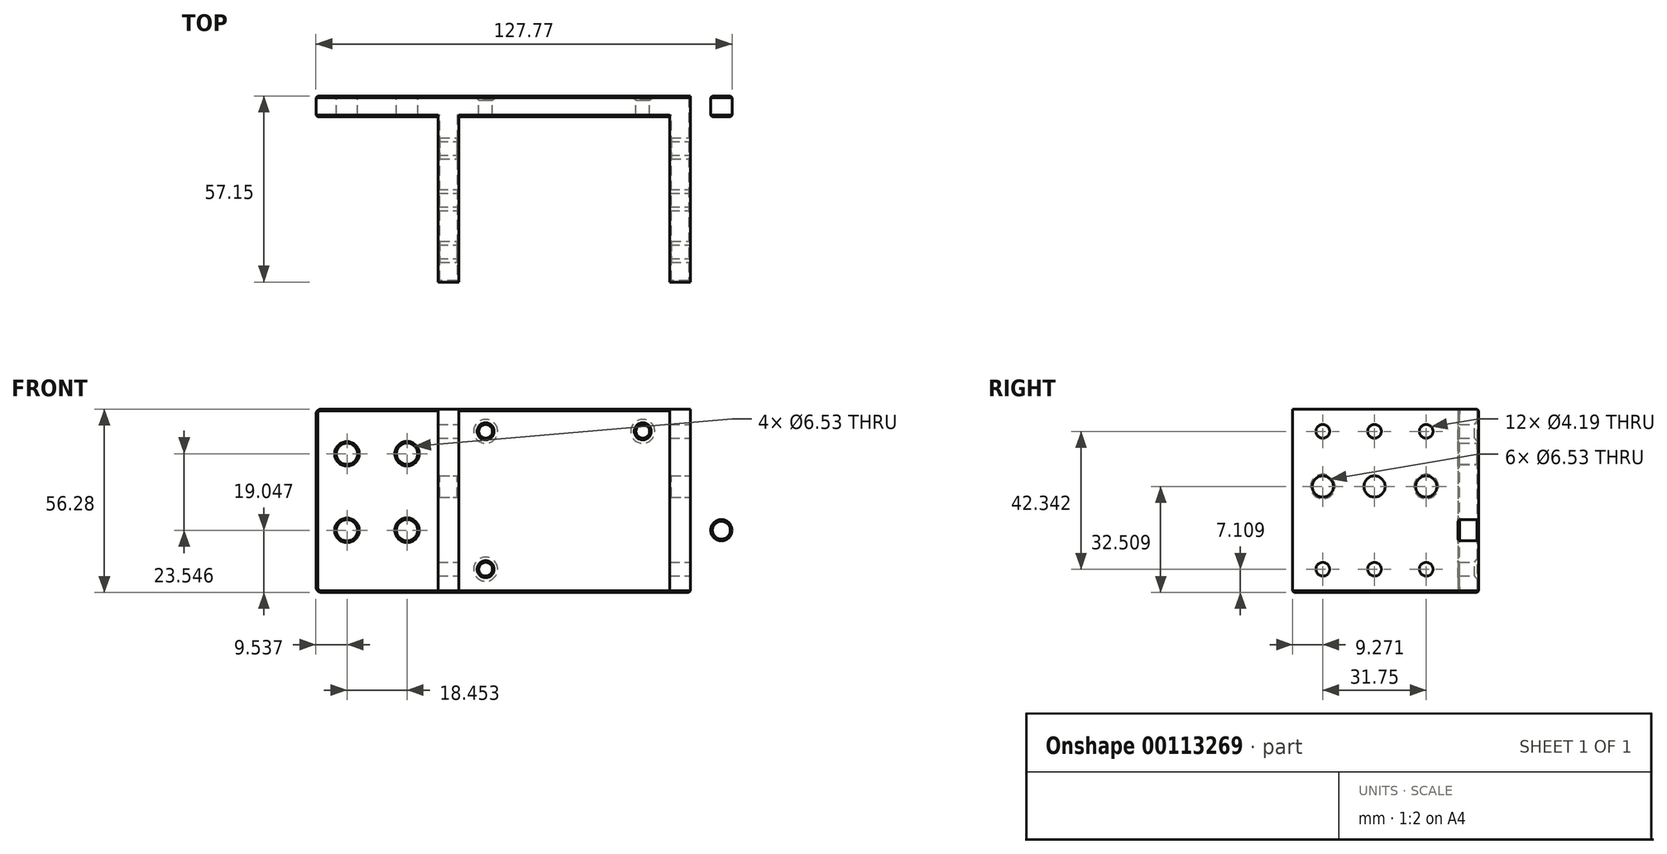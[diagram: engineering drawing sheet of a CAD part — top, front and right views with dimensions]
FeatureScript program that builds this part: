
annotation { "Feature Type Name" : "Feature", "Feature Type Description" : "" }
export const myFeature = defineFeature(function(context is Context, id is Id, definition is map)
    precondition{}
    {
        {
            var Q0;
            Q0=qCreatedBy(makeId("Front.planeOp"),FACE);
            var sketch = newSketch(context, id + "F0", { "sketchPlane" : qUnion([Q0])});
            skLineSegment(sketch, "E0.right", {"start": v(-76.2, -28.14) * mm, "end": v(-76.25, 28.14) * mm});
            skCircle(sketch, "E1", {"center": v(-24.13, 21.31) * mm, "radius": 2.1 * mm});
            skCircle(sketch, "E2", {"center": v(-24.13, -21.03) * mm, "radius": 2.1 * mm});
            skCircle(sketch, "E3", {"center": v(-66.71, -9.1) * mm, "radius": 3.26 * mm});
            skCircle(sketch, "E4", {"center": v(-66.71, 14.4) * mm, "radius": 3.26 * mm});
            skCircle(sketch, "E5", {"center": v(-48.26, -9.04) * mm, "radius": 3.26 * mm});
            skCircle(sketch, "E6", {"center": v(-48.26, 14.45) * mm, "radius": 3.26 * mm});
            skLineSegment(sketch, "E7.bottom", {"start": v(-38.74, 28.14) * mm, "end": v(-32.39, 28.14) * mm});
            skLineSegment(sketch, "E7.top", {"start": v(-38.74, -28.14) * mm, "end": v(-32.39, -28.14) * mm});
            skLineSegment(sketch, "E7.left", {"start": v(-38.74, 28.14) * mm, "end": v(-38.74, -28.14) * mm});
            skLineSegment(sketch, "E7.right", {"start": v(-32.39, 28.14) * mm, "end": v(-32.39, -28.14) * mm});
            skLineSegment(sketch, "E8.trimOffspring", {"start": v(-32.39, 28.14) * mm, "end": v(-76.25, 28.14) * mm});
            skLineSegment(sketch, "E9.trimOffspring", {"start": v(-32.39, -28.14) * mm, "end": v(-76.2, -28.14) * mm});
            skLineSegment(sketch, "E10.bottom", {"start": v(-32.39, 28.14) * mm, "end": v(0, 28.14) * mm});
            skLineSegment(sketch, "E10.top", {"start": v(-32.39, -28.14) * mm, "end": v(0, -28.14) * mm});
            skLineSegment(sketch, "E11.MirrorCS", {"start": v(38.74, -28.14) * mm, "end": v(32.39, -28.14) * mm});
            skLineSegment(sketch, "E12.MirrorCS", {"start": v(38.74, 28.14) * mm, "end": v(32.39, 28.14) * mm});
            skCircle(sketch, "E13.MirrorC", {"center": v(48.26, -9.04) * mm, "radius": 3.26 * mm});
            skCircle(sketch, "E14.MirrorC", {"center": v(66.71, 14.4) * mm, "radius": 3.26 * mm});
            skCircle(sketch, "E15.MirrorC", {"center": v(66.71, -9.1) * mm, "radius": 3.26 * mm});
            skCircle(sketch, "E16.MirrorC", {"center": v(24.13, -21.03) * mm, "radius": 2.1 * mm});
            skCircle(sketch, "E17.MirrorC", {"center": v(48.26, 14.45) * mm, "radius": 3.26 * mm});
            skLineSegment(sketch, "E18.MirrorCS", {"start": v(32.39, 28.14) * mm, "end": v(32.39, -28.14) * mm});
            skCircle(sketch, "E19.MirrorC", {"center": v(24.13, 21.31) * mm, "radius": 2.1 * mm});
            skLineSegment(sketch, "E20.MirrorCS", {"start": v(38.74, 28.14) * mm, "end": v(38.74, -28.14) * mm});
            skLineSegment(sketch, "E21.MirrorCS", {"start": v(32.39, 28.14) * mm, "end": v(0, 28.14) * mm});
            skLineSegment(sketch, "E22.MirrorCS", {"start": v(32.39, -28.14) * mm, "end": v(0, -28.14) * mm});
            skLineSegment(sketch, "E23.MirrorCS", {"start": v(32.39, 28.14) * mm, "end": v(76.25, 28.14) * mm});
            skLineSegment(sketch, "E24.MirrorCS", {"start": v(32.39, -28.14) * mm, "end": v(76.2, -28.14) * mm});
            skLineSegment(sketch, "E25.MirrorCS", {"start": v(76.2, -28.14) * mm, "end": v(76.25, 28.14) * mm});
            skSolve(sketch);
        }
        {
            var Q0;
            {var subQ0=sQuery(id+"F0.wireOp",EDGE,"E7.left");Q0=makeQuery(id+"F0.imprint","IMPRINT",FACE,{"disambiguationData":[TD([[makeQuery(id+"F0.imprint","IMPRINT",EDGE,{"derivedFrom":subQ0}),1.0]])]});}
            var Q1;
            {var subQ0=sQuery(id+"F0.wireOp",EDGE,"E18.MirrorCS");Q1=makeQuery(id+"F0.imprint","IMPRINT",FACE,{"disambiguationData":[TD([[makeQuery(id+"F0.imprint","IMPRINT",EDGE,{"derivedFrom":subQ0}),1.0]])]});}
            extrude(context, id + "F1", {"entities" : qUnion([Q0, Q1]), "depth" : 57.15 * mm});
        }
        {
            var Q0;
            {var subQ0=sQuery(id+"F0.wireOp",EDGE,"E0.right");Q0=makeQuery(id+"F0.imprint","IMPRINT",FACE,{"disambiguationData":[TD([[makeQuery(id+"F0.imprint","IMPRINT",EDGE,{"derivedFrom":subQ0}),-1.0]])]});}
            var Q1;
            Q1=makeQuery(id+"F0.imprint","IMPRINT",FACE,{"disambiguationData":[TD([[makeQuery(id+"F0.imprint","IMPRINT",EDGE,{"derivedFrom":sQuery(id+"F0.wireOp",EDGE,"E1")}),-1.0]])]});
            var Q2;
            Q2=makeQuery(id+"F0.imprint","IMPRINT",FACE,{"disambiguationData":[TD([[makeQuery(id+"F0.imprint","IMPRINT",EDGE,{"derivedFrom":sQuery(id+"F0.wireOp",EDGE,"E16.MirrorC")}),1.0]])]});
            var Q3;
            Q3=makeQuery(id+"F0.imprint","IMPRINT",FACE,{"disambiguationData":[TD([[makeQuery(id+"F0.imprint","IMPRINT",EDGE,{"derivedFrom":sQuery(id+"F0.wireOp",EDGE,"E13.MirrorC")}),1.0]])]});
            extrude(context, id + "F2", {"entities" : qUnion([Q0, Q1, Q2, Q3]), "depth" : 6.35 * mm});
        }
        {
            var Q0;
            Q0=makeQuery(id+"F1.opExtrude","SWEPT_BODY",BODY,{"disambiguationData":[OSD([sQuery(id+"F0.wireOp",EDGE,"E18.MirrorCS"),sQuery(id+"F0.wireOp",EDGE,"E20.MirrorCS"),sQuery(id+"F0.wireOp",EDGE,"E23.MirrorCS"),sQuery(id+"F0.wireOp",EDGE,"E24.MirrorCS")])]});
            var Q1;
            Q1=makeQuery(id+"F2.opExtrude","SWEPT_BODY",BODY,{"disambiguationData":[OSD([sQuery(id+"F0.wireOp",EDGE,"E0.right"),sQuery(id+"F0.wireOp",EDGE,"E3"),sQuery(id+"F0.wireOp",EDGE,"E4"),sQuery(id+"F0.wireOp",EDGE,"E5"),sQuery(id+"F0.wireOp",EDGE,"E6"),sQuery(id+"F0.wireOp",EDGE,"E7.left"),sQuery(id+"F0.wireOp",EDGE,"E8.trimOffspring"),sQuery(id+"F0.wireOp",EDGE,"E9.trimOffspring")])]});
            var Q2;
            Q2=makeQuery(id+"F1.opExtrude","SWEPT_BODY",BODY,{"disambiguationData":[OSD([sQuery(id+"F0.wireOp",EDGE,"E7.left"),sQuery(id+"F0.wireOp",EDGE,"E8.trimOffspring"),sQuery(id+"F0.wireOp",EDGE,"E9.trimOffspring"),sQuery(id+"F0.wireOp",EDGE,"E7.right")])]});
            var Q3;
            Q3=makeQuery(id+"F2.opExtrude","SWEPT_BODY",BODY,{"disambiguationData":[OSD([sQuery(id+"F0.wireOp",EDGE,"E1"),sQuery(id+"F0.wireOp",EDGE,"E2"),sQuery(id+"F0.wireOp",EDGE,"E10.bottom"),sQuery(id+"F0.wireOp",EDGE,"E10.top"),sQuery(id+"F0.wireOp",EDGE,"E7.right"),sQuery(id+"F0.wireOp",EDGE,"E16.MirrorC"),sQuery(id+"F0.wireOp",EDGE,"E19.MirrorC"),sQuery(id+"F0.wireOp",EDGE,"E18.MirrorCS"),sQuery(id+"F0.wireOp",EDGE,"E21.MirrorCS"),sQuery(id+"F0.wireOp",EDGE,"E22.MirrorCS")])]});
            var Q4;
            Q4=makeQuery(id+"F2.opExtrude","SWEPT_BODY",BODY,{"disambiguationData":[OSD([sQuery(id+"F0.wireOp",EDGE,"E13.MirrorC"),sQuery(id+"F0.wireOp",EDGE,"E14.MirrorC"),sQuery(id+"F0.wireOp",EDGE,"E15.MirrorC"),sQuery(id+"F0.wireOp",EDGE,"E17.MirrorC"),sQuery(id+"F0.wireOp",EDGE,"E20.MirrorCS"),sQuery(id+"F0.wireOp",EDGE,"E23.MirrorCS"),sQuery(id+"F0.wireOp",EDGE,"E24.MirrorCS"),sQuery(id+"F0.wireOp",EDGE,"E25.MirrorCS")])]});
            booleanBodies(context, id + "F3", {"operationType" : BooleanOperationType.UNION, "tools" : qUnion([Q0, Q1, Q2, Q3, Q4])});
        }
        {
            var Q0;
            Q0=makeQuery(id+"F2.opExtrude","CAP_EDGE",EDGE,{"disambiguationData":[OSD([sQuery(id+"F0.wireOp",EDGE,"E19.MirrorC")])],"isStart":true});
            var Q1;
            Q1=makeQuery(id+"F2.opExtrude","CAP_EDGE",EDGE,{"disambiguationData":[OSD([sQuery(id+"F0.wireOp",EDGE,"E1")])],"isStart":true});
            var Q2;
            Q2=makeQuery(id+"F2.opExtrude","CAP_EDGE",EDGE,{"disambiguationData":[OSD([sQuery(id+"F0.wireOp",EDGE,"E16.MirrorC")])],"isStart":true});
            var Q3;
            Q3=makeQuery(id+"F2.opExtrude","CAP_EDGE",EDGE,{"disambiguationData":[OSD([sQuery(id+"F0.wireOp",EDGE,"E2")])],"isStart":true});
            chamfer(context, id + "F4", {"entities" : qUnion([Q0, Q1, Q2, Q3]), "chamferType" : ChamferType.TWO_OFFSETS, "width1" : 1.59 * mm, "oppositeDirection" : false, "width2" : 1.27 * mm, "tangentPropagation" : true});
        }
        {
            var Q0;
            Q0=makeQuery(id+"F2.opExtrude","SWEPT_EDGE",EDGE,{"disambiguationData":[OSD([sQuery(id+"F0.wireOp",EDGE,"E23.MirrorCS"),sQuery(id+"F0.wireOp",EDGE,"E25.MirrorCS")])]});
            var Q1;
            Q1=makeQuery(id+"F2.opExtrude","SWEPT_EDGE",EDGE,{"disambiguationData":[OSD([sQuery(id+"F0.wireOp",EDGE,"E0.right"),sQuery(id+"F0.wireOp",EDGE,"E8.trimOffspring")])]});
            var Q2;
            Q2=makeQuery(id+"F2.opExtrude","SWEPT_EDGE",EDGE,{"disambiguationData":[OSD([sQuery(id+"F0.wireOp",EDGE,"E24.MirrorCS"),sQuery(id+"F0.wireOp",EDGE,"E25.MirrorCS")])]});
            var Q3;
            Q3=makeQuery(id+"F2.opExtrude","SWEPT_EDGE",EDGE,{"disambiguationData":[OSD([sQuery(id+"F0.wireOp",EDGE,"E0.right"),sQuery(id+"F0.wireOp",EDGE,"E9.trimOffspring")])]});
            var Q4;
            Q4=makeQuery(id+"F1.opExtrude","CAP_EDGE",EDGE,{"disambiguationData":[OSD([sQuery(id+"F0.wireOp",EDGE,"E8.trimOffspring")])],"isStart":false});
            var Q5;
            Q5=makeQuery(id+"F1.opExtrude","CAP_EDGE",EDGE,{"disambiguationData":[OSD([sQuery(id+"F0.wireOp",EDGE,"E9.trimOffspring")])],"isStart":false});
            var Q6;
            Q6=makeQuery(id+"F1.opExtrude","CAP_EDGE",EDGE,{"disambiguationData":[OSD([sQuery(id+"F0.wireOp",EDGE,"E23.MirrorCS")])],"isStart":false});
            var Q7;
            Q7=makeQuery(id+"F1.opExtrude","CAP_EDGE",EDGE,{"disambiguationData":[OSD([sQuery(id+"F0.wireOp",EDGE,"E24.MirrorCS")])],"isStart":false});
            fillet(context, id + "F5", {"entities" : qUnion([Q0, Q1, Q2, Q3, Q4, Q5, Q6, Q7]), "radius" : 1.6 * mm, "tangentPropagation" : true, "allowEdgeOverflow" : false});
        }
        {
            var Q0;
            Q0=makeQuery(id+"F2.opExtrude","CAP_EDGE",EDGE,{"disambiguationData":[OSD([sQuery(id+"F0.wireOp",EDGE,"E14.MirrorC")])],"isStart":true});
            var Q1;
            Q1=makeQuery(id+"F2.opExtrude","CAP_EDGE",EDGE,{"disambiguationData":[OSD([sQuery(id+"F0.wireOp",EDGE,"E17.MirrorC")])],"isStart":true});
            var Q2;
            Q2=makeQuery(id+"F2.opExtrude","CAP_EDGE",EDGE,{"disambiguationData":[OSD([sQuery(id+"F0.wireOp",EDGE,"E15.MirrorC")])],"isStart":true});
            var Q3;
            Q3=makeQuery(id+"F2.opExtrude","CAP_EDGE",EDGE,{"disambiguationData":[OSD([sQuery(id+"F0.wireOp",EDGE,"E13.MirrorC")])],"isStart":true});
            var Q4;
            Q4=makeQuery(id+"F2.opExtrude","CAP_EDGE",EDGE,{"disambiguationData":[OSD([sQuery(id+"F0.wireOp",EDGE,"E6")])],"isStart":true});
            var Q5;
            Q5=makeQuery(id+"F2.opExtrude","CAP_EDGE",EDGE,{"disambiguationData":[OSD([sQuery(id+"F0.wireOp",EDGE,"E4")])],"isStart":true});
            var Q6;
            Q6=makeQuery(id+"F2.opExtrude","CAP_EDGE",EDGE,{"disambiguationData":[OSD([sQuery(id+"F0.wireOp",EDGE,"E3")])],"isStart":true});
            var Q7;
            Q7=makeQuery(id+"F2.opExtrude","CAP_EDGE",EDGE,{"disambiguationData":[OSD([sQuery(id+"F0.wireOp",EDGE,"E5")])],"isStart":true});
            var Q8;
            Q8=makeQuery(id+"F2.opExtrude","CAP_EDGE",EDGE,{"disambiguationData":[OSD([sQuery(id+"F0.wireOp",EDGE,"E25.MirrorCS")])],"isStart":true});
            var Q9;
            Q9=makeQuery(id+"F2.opExtrude","CAP_EDGE",EDGE,{"disambiguationData":[OSD([sQuery(id+"F0.wireOp",EDGE,"E8.trimOffspring")])],"isStart":false});
            var Q10;
            Q10=makeQuery(id+"F2.opExtrude","CAP_EDGE",EDGE,{"disambiguationData":[OSD([sQuery(id+"F0.wireOp",EDGE,"E10.bottom"),sQuery(id+"F0.wireOp",EDGE,"E21.MirrorCS")])],"isStart":false});
            var Q11;
            Q11=makeQuery(id+"F2.opExtrude","CAP_EDGE",EDGE,{"disambiguationData":[OSD([sQuery(id+"F0.wireOp",EDGE,"E25.MirrorCS")])],"isStart":false});
            var Q12;
            Q12=makeQuery(id+"F2.opExtrude","CAP_EDGE",EDGE,{"disambiguationData":[OSD([sQuery(id+"F0.wireOp",EDGE,"E10.top"),sQuery(id+"F0.wireOp",EDGE,"E22.MirrorCS")])],"isStart":false});
            var Q13;
            {var subQ0=sQuery(id+"F0.wireOp",EDGE,"E24.MirrorCS");var subQ1=sQuery(id+"F0.wireOp",EDGE,"E9.trimOffspring");Q13=makeQuery(id+"F3.opBoolean","MERGE",FACE,{"derivedFrom":[makeQuery(id+"F1.opExtrude","SWEPT_FACE",FACE,{"disambiguationData":[OSD([subQ1])]}),makeQuery(id+"F1.opExtrude","SWEPT_FACE",FACE,{"disambiguationData":[OSD([subQ0])]}),makeQuery(id+"F2.opExtrude","SWEPT_FACE",FACE,{"disambiguationData":[OSD([subQ1])]}),makeQuery(id+"F2.opExtrude","SWEPT_FACE",FACE,{"disambiguationData":[OSD([sQuery(id+"F0.wireOp",EDGE,"E10.top"),sQuery(id+"F0.wireOp",EDGE,"E22.MirrorCS")])]}),makeQuery(id+"F2.opExtrude","SWEPT_FACE",FACE,{"disambiguationData":[OSD([subQ0])]})]});}
            var Q14;
            Q14=makeQuery(id+"F2.opExtrude","CAP_EDGE",EDGE,{"disambiguationData":[OSD([sQuery(id+"F0.wireOp",EDGE,"E23.MirrorCS")])],"isStart":false});
            var Q15;
            Q15=makeQuery(id+"F2.opExtrude","CAP_EDGE",EDGE,{"disambiguationData":[OSD([sQuery(id+"F0.wireOp",EDGE,"E4")])],"isStart":false});
            var Q16;
            Q16=makeQuery(id+"F2.opExtrude","CAP_EDGE",EDGE,{"disambiguationData":[OSD([sQuery(id+"F0.wireOp",EDGE,"E6")])],"isStart":false});
            var Q17;
            Q17=makeQuery(id+"F2.opExtrude","CAP_EDGE",EDGE,{"disambiguationData":[OSD([sQuery(id+"F0.wireOp",EDGE,"E3")])],"isStart":false});
            var Q18;
            Q18=makeQuery(id+"F2.opExtrude","CAP_EDGE",EDGE,{"disambiguationData":[OSD([sQuery(id+"F0.wireOp",EDGE,"E5")])],"isStart":false});
            var Q19;
            Q19=makeQuery(id+"F2.opExtrude","CAP_EDGE",EDGE,{"disambiguationData":[OSD([sQuery(id+"F0.wireOp",EDGE,"E1")])],"isStart":false});
            var Q20;
            Q20=makeQuery(id+"F2.opExtrude","CAP_EDGE",EDGE,{"disambiguationData":[OSD([sQuery(id+"F0.wireOp",EDGE,"E19.MirrorC")])],"isStart":false});
            var Q21;
            Q21=makeQuery(id+"F2.opExtrude","CAP_EDGE",EDGE,{"disambiguationData":[OSD([sQuery(id+"F0.wireOp",EDGE,"E2")])],"isStart":false});
            var Q22;
            Q22=makeQuery(id+"F2.opExtrude","CAP_EDGE",EDGE,{"disambiguationData":[OSD([sQuery(id+"F0.wireOp",EDGE,"E16.MirrorC")])],"isStart":false});
            var Q23;
            Q23=makeQuery(id+"F2.opExtrude","CAP_EDGE",EDGE,{"disambiguationData":[OSD([sQuery(id+"F0.wireOp",EDGE,"E17.MirrorC")])],"isStart":false});
            var Q24;
            Q24=makeQuery(id+"F2.opExtrude","CAP_EDGE",EDGE,{"disambiguationData":[OSD([sQuery(id+"F0.wireOp",EDGE,"E14.MirrorC")])],"isStart":false});
            var Q25;
            Q25=makeQuery(id+"F2.opExtrude","CAP_EDGE",EDGE,{"disambiguationData":[OSD([sQuery(id+"F0.wireOp",EDGE,"E13.MirrorC")])],"isStart":false});
            var Q26;
            Q26=makeQuery(id+"F2.opExtrude","CAP_EDGE",EDGE,{"disambiguationData":[OSD([sQuery(id+"F0.wireOp",EDGE,"E15.MirrorC")])],"isStart":false});
            chamfer(context, id + "F6", {"entities" : qUnion([Q0, Q1, Q2, Q3, Q4, Q5, Q6, Q7, Q8, Q9, Q10, Q11, Q12, Q13, Q14, Q15, Q16, Q17, Q18, Q19, Q20, Q21, Q22, Q23, Q24, Q25, Q26]), "width" : 0.5 * mm, "tangentPropagation" : true});
        }
        {
            var Q0;
            Q0=makeQuery(id+"F1.opExtrude","SWEPT_FACE",FACE,{"disambiguationData":[OSD([sQuery(id+"F0.wireOp",EDGE,"E20.MirrorCS")])]});
            var sketch = newSketch(context, id + "F7", { "sketchPlane" : qUnion([Q0])});
            skPoint(sketch, "E26.centerSnap0", {"position": v(-30.95, -27.64) * mm});
            skPoint(sketch, "E26.centerSnap1", {"position": v(-56.64, 0) * mm});
            skCircle(sketch, "E27", {"center": v(-47.88, 4.37) * mm, "radius": 3.26 * mm});
            skCircle(sketch, "E28", {"center": v(-16.13, 4.37) * mm, "radius": 3.26 * mm});
            skCircle(sketch, "E29", {"center": v(-47.88, 21.31) * mm, "radius": 2.1 * mm});
            skCircle(sketch, "E30", {"center": v(-16.13, 21.31) * mm, "radius": 2.1 * mm});
            skCircle(sketch, "E31", {"center": v(-32, 21.31) * mm, "radius": 2.1 * mm});
            skCircle(sketch, "E32", {"center": v(-47.88, -21.03) * mm, "radius": 2.1 * mm});
            skCircle(sketch, "E33", {"center": v(-32, -21.03) * mm, "radius": 2.1 * mm});
            skCircle(sketch, "E34", {"center": v(-16.13, -21.03) * mm, "radius": 2.1 * mm});
            skCircle(sketch, "E35", {"center": v(-32, 4.37) * mm, "radius": 3.26 * mm});
            skSolve(sketch);
        }
        {
            var Q0;
            Q0 = qSketchRegion(id + "F7", true);
            extrude(context, id + "F8", {"entities" : qUnion([Q0]), "operationType" : NewBodyOperationType.REMOVE, "endBound" : BoundingType.THROUGH_ALL, "oppositeDirection" : true, "depth" : 152.4 * mm});
        }
        {
            var Q0;
            Q0=makeQuery(id+"F8.boolean.opBoolean","COPY",EDGE,{"derivedFrom":makeQuery(id+"F8.opExtrude","CAP_EDGE",EDGE,{"disambiguationData":[OSD([sQuery(id+"F7.wireOp",EDGE,"E27")])],"isStart":true})});
            var Q1;
            Q1=makeQuery(id+"F8.boolean.opBoolean","COPY",EDGE,{"derivedFrom":makeQuery(id+"F8.opExtrude","CAP_EDGE",EDGE,{"disambiguationData":[OSD([sQuery(id+"F7.wireOp",EDGE,"E26")])],"isStart":true})});
            var Q2;
            Q2=makeQuery(id+"F8.boolean.opBoolean","COPY",EDGE,{"derivedFrom":makeQuery(id+"F8.opExtrude","CAP_EDGE",EDGE,{"disambiguationData":[OSD([sQuery(id+"F7.wireOp",EDGE,"E28")])],"isStart":true})});
            var Q3;
            Q3=makeQuery(id+"F8.boolean.opBoolean","INTERSECT",EDGE,{"derivedFrom":[makeQuery(id+"F1.opExtrude","SWEPT_FACE",FACE,{"disambiguationData":[OSD([sQuery(id+"F0.wireOp",EDGE,"E18.MirrorCS")])]}),makeQuery(id+"F8.opExtrude","SWEPT_FACE",FACE,{"disambiguationData":[OSD([sQuery(id+"F7.wireOp",EDGE,"E27")])]})]});
            var Q4;
            Q4=makeQuery(id+"F8.boolean.opBoolean","INTERSECT",EDGE,{"derivedFrom":[makeQuery(id+"F1.opExtrude","SWEPT_FACE",FACE,{"disambiguationData":[OSD([sQuery(id+"F0.wireOp",EDGE,"E18.MirrorCS")])]}),makeQuery(id+"F8.opExtrude","SWEPT_FACE",FACE,{"disambiguationData":[OSD([sQuery(id+"F7.wireOp",EDGE,"E26")])]})]});
            var Q5;
            Q5=makeQuery(id+"F8.boolean.opBoolean","INTERSECT",EDGE,{"derivedFrom":[makeQuery(id+"F1.opExtrude","SWEPT_FACE",FACE,{"disambiguationData":[OSD([sQuery(id+"F0.wireOp",EDGE,"E18.MirrorCS")])]}),makeQuery(id+"F8.opExtrude","SWEPT_FACE",FACE,{"disambiguationData":[OSD([sQuery(id+"F7.wireOp",EDGE,"E28")])]})]});
            var Q6;
            Q6=makeQuery(id+"F8.boolean.opBoolean","INTERSECT",EDGE,{"derivedFrom":[makeQuery(id+"F1.opExtrude","SWEPT_FACE",FACE,{"disambiguationData":[OSD([sQuery(id+"F0.wireOp",EDGE,"E7.right")])]}),makeQuery(id+"F8.opExtrude","SWEPT_FACE",FACE,{"disambiguationData":[OSD([sQuery(id+"F7.wireOp",EDGE,"E27")])]})]});
            var Q7;
            Q7=makeQuery(id+"F8.boolean.opBoolean","INTERSECT",EDGE,{"derivedFrom":[makeQuery(id+"F1.opExtrude","SWEPT_FACE",FACE,{"disambiguationData":[OSD([sQuery(id+"F0.wireOp",EDGE,"E7.right")])]}),makeQuery(id+"F8.opExtrude","SWEPT_FACE",FACE,{"disambiguationData":[OSD([sQuery(id+"F7.wireOp",EDGE,"E26")])]})]});
            var Q8;
            Q8=makeQuery(id+"F8.boolean.opBoolean","INTERSECT",EDGE,{"derivedFrom":[makeQuery(id+"F1.opExtrude","SWEPT_FACE",FACE,{"disambiguationData":[OSD([sQuery(id+"F0.wireOp",EDGE,"E7.right")])]}),makeQuery(id+"F8.opExtrude","SWEPT_FACE",FACE,{"disambiguationData":[OSD([sQuery(id+"F7.wireOp",EDGE,"E28")])]})]});
            var Q9;
            Q9=makeQuery(id+"F8.boolean.opBoolean","INTERSECT",EDGE,{"derivedFrom":[makeQuery(id+"F1.opExtrude","SWEPT_FACE",FACE,{"disambiguationData":[OSD([sQuery(id+"F0.wireOp",EDGE,"E7.left")])]}),makeQuery(id+"F8.opExtrude","SWEPT_FACE",FACE,{"disambiguationData":[OSD([sQuery(id+"F7.wireOp",EDGE,"E27")])]})]});
            var Q10;
            Q10=makeQuery(id+"F8.boolean.opBoolean","INTERSECT",EDGE,{"derivedFrom":[makeQuery(id+"F1.opExtrude","SWEPT_FACE",FACE,{"disambiguationData":[OSD([sQuery(id+"F0.wireOp",EDGE,"E7.left")])]}),makeQuery(id+"F8.opExtrude","SWEPT_FACE",FACE,{"disambiguationData":[OSD([sQuery(id+"F7.wireOp",EDGE,"E26")])]})]});
            var Q11;
            Q11=makeQuery(id+"F8.boolean.opBoolean","INTERSECT",EDGE,{"derivedFrom":[makeQuery(id+"F1.opExtrude","SWEPT_FACE",FACE,{"disambiguationData":[OSD([sQuery(id+"F0.wireOp",EDGE,"E7.left")])]}),makeQuery(id+"F8.opExtrude","SWEPT_FACE",FACE,{"disambiguationData":[OSD([sQuery(id+"F7.wireOp",EDGE,"E28")])]})]});
            var Q12;
            Q12=makeQuery(id+"F8.boolean.opBoolean","COPY",EDGE,{"derivedFrom":makeQuery(id+"F8.opExtrude","CAP_EDGE",EDGE,{"disambiguationData":[OSD([sQuery(id+"F7.wireOp",EDGE,"E29")])],"isStart":true})});
            var Q13;
            Q13=makeQuery(id+"F8.boolean.opBoolean","COPY",EDGE,{"derivedFrom":makeQuery(id+"F8.opExtrude","CAP_EDGE",EDGE,{"disambiguationData":[OSD([sQuery(id+"F7.wireOp",EDGE,"E31")])],"isStart":true})});
            var Q14;
            Q14=makeQuery(id+"F8.boolean.opBoolean","COPY",EDGE,{"derivedFrom":makeQuery(id+"F8.opExtrude","CAP_EDGE",EDGE,{"disambiguationData":[OSD([sQuery(id+"F7.wireOp",EDGE,"E30")])],"isStart":true})});
            var Q15;
            Q15=makeQuery(id+"F8.boolean.opBoolean","COPY",EDGE,{"derivedFrom":makeQuery(id+"F8.opExtrude","CAP_EDGE",EDGE,{"disambiguationData":[OSD([sQuery(id+"F7.wireOp",EDGE,"E32")])],"isStart":true})});
            var Q16;
            Q16=makeQuery(id+"F8.boolean.opBoolean","COPY",EDGE,{"derivedFrom":makeQuery(id+"F8.opExtrude","CAP_EDGE",EDGE,{"disambiguationData":[OSD([sQuery(id+"F7.wireOp",EDGE,"E33")])],"isStart":true})});
            var Q17;
            Q17=makeQuery(id+"F8.boolean.opBoolean","COPY",EDGE,{"derivedFrom":makeQuery(id+"F8.opExtrude","CAP_EDGE",EDGE,{"disambiguationData":[OSD([sQuery(id+"F7.wireOp",EDGE,"E34")])],"isStart":true})});
            var Q18;
            Q18=makeQuery(id+"F8.boolean.opBoolean","COPY",EDGE,{"derivedFrom":makeQuery(id+"F8.opExtrude","CAP_EDGE",EDGE,{"disambiguationData":[OSD([sQuery(id+"F7.wireOp",EDGE,"E35")])],"isStart":true})});
            chamfer(context, id + "F9", {"entities" : qUnion([Q0, Q1, Q2, Q3, Q4, Q5, Q6, Q7, Q8, Q9, Q10, Q11, Q12, Q13, Q14, Q15, Q16, Q17, Q18]), "width" : 0.5 * mm, "tangentPropagation" : true});
        }
    });
